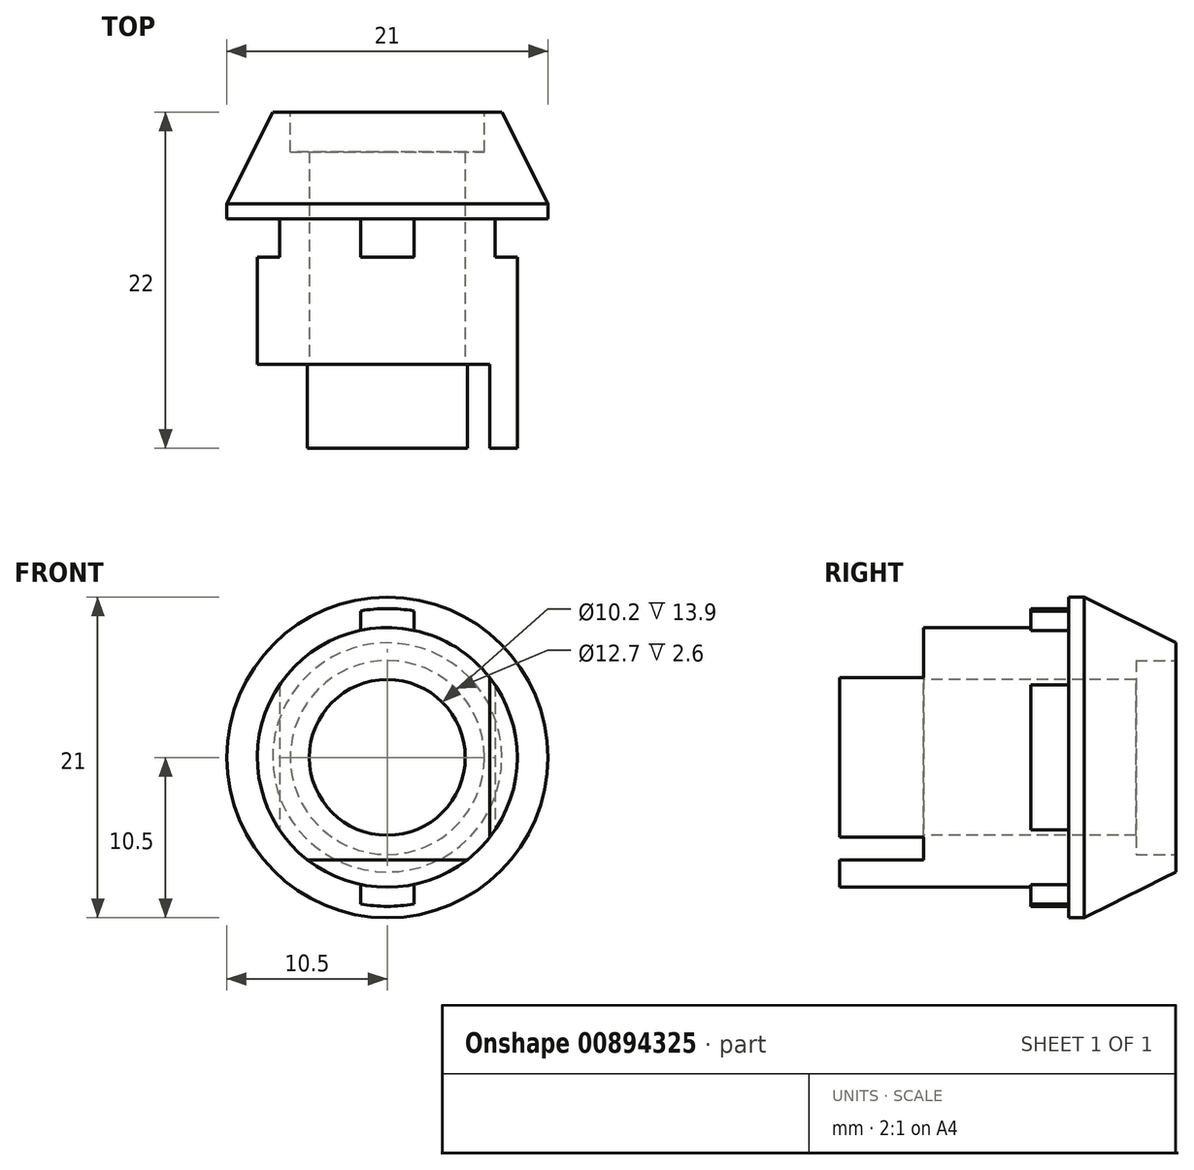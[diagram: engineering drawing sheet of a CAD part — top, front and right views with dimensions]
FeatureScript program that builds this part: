
annotation { "Feature Type Name" : "Feature", "Feature Type Description" : "" }
export const myFeature = defineFeature(function(context is Context, id is Id, definition is map)
    precondition{}
    {
        {
            var Q0;
            Q0=qCreatedBy(makeId("Front.planeOp"),FACE);
            var sketch = newSketch(context, id + "F0", { "sketchPlane" : qUnion([Q0])});
            skCircle(sketch, "E0", {"center": v(0, 0) * mm, "radius": 5.1 * mm});
            skCircle(sketch, "E1", {"center": v(0, 0) * mm, "radius": 10.5 * mm});
            skCircle(sketch, "E2", {"center": v(0, 0) * mm, "radius": 9.75 * mm});
            skCircle(sketch, "E3", {"center": v(0, 0) * mm, "radius": 8.5 * mm});
            skLineSegment(sketch, "E4", {"start": v(-1.75, 9.6) * mm, "end": v(-1.75, 8.32) * mm});
            skLineSegment(sketch, "E5.MirrorCS", {"start": v(1.75, 9.6) * mm, "end": v(1.75, 8.32) * mm});
            skLineSegment(sketch, "E6.MirrorCS", {"start": v(-1.75, -9.6) * mm, "end": v(-1.75, -8.32) * mm});
            skLineSegment(sketch, "E7.MirrorCS", {"start": v(1.75, -9.6) * mm, "end": v(1.75, -8.32) * mm});
            skLineSegment(sketch, "E8", {"start": v(7.05, 4.75) * mm, "end": v(7.05, -4.75) * mm});
            skLineSegment(sketch, "E9.MirrorCS", {"start": v(-7.05, 4.75) * mm, "end": v(-7.05, -4.75) * mm});
            skLineSegment(sketch, "E10", {"start": v(-5.23, -6.7) * mm, "end": v(5.23, -6.7) * mm});
            skLineSegment(sketch, "E11", {"start": v(6.7, -5.23) * mm, "end": v(6.7, 5.23) * mm});
            skSolve(sketch);
        }
        {
            var Q0;
            Q0=makeQuery(id+"F0.imprint","IMPRINT",FACE,{"disambiguationData":[TD([[makeQuery(id+"F0.imprint","IMPRINT",EDGE,{"derivedFrom":sQuery(id+"F0.wireOp",EDGE,"E1")}),1.0]])]});
            var Q1;
            {var subQ5=sQuery(id+"F0.wireOp",EDGE,"E4");Q1=makeQuery(id+"F0.imprint","IMPRINT",FACE,{"disambiguationData":[TD([[makeQuery(id+"F0.imprint","IMPRINT",EDGE,{"derivedFrom":subQ5}),-1.0]])]});}
            var Q2;
            {var subQ0=sQuery(id+"F0.wireOp",EDGE,"E4");Q2=makeQuery(id+"F0.imprint","IMPRINT",FACE,{"disambiguationData":[TD([[makeQuery(id+"F0.imprint","IMPRINT",EDGE,{"derivedFrom":subQ0}),1.0]])]});}
            var Q3;
            {var subQ3=sQuery(id+"F0.wireOp",EDGE,"E5.MirrorCS");Q3=makeQuery(id+"F0.imprint","IMPRINT",FACE,{"disambiguationData":[TD([[makeQuery(id+"F0.imprint","IMPRINT",EDGE,{"derivedFrom":subQ3}),1.0]])]});}
            var Q4;
            {var subQ0=sQuery(id+"F0.wireOp",EDGE,"E6.MirrorCS");Q4=makeQuery(id+"F0.imprint","IMPRINT",FACE,{"disambiguationData":[TD([[makeQuery(id+"F0.imprint","IMPRINT",EDGE,{"derivedFrom":subQ0}),-1.0]])]});}
            var Q5;
            {var subQ2=sQuery(id+"F0.wireOp",EDGE,"E10");Q5=makeQuery(id+"F0.imprint","IMPRINT",FACE,{"disambiguationData":[TD([[makeQuery(id+"F0.imprint","IMPRINT",EDGE,{"derivedFrom":subQ2}),-1.0]])]});}
            var Q6;
            {var subQ0=sQuery(id+"F0.wireOp",EDGE,"E9.MirrorCS");Q6=makeQuery(id+"F0.imprint","IMPRINT",FACE,{"disambiguationData":[TD([[makeQuery(id+"F0.imprint","IMPRINT",EDGE,{"derivedFrom":subQ0}),-1.0]])]});}
            var Q7;
            Q7=makeQuery(id+"F0.imprint","IMPRINT",FACE,{"disambiguationData":[TD([[makeQuery(id+"F0.imprint","IMPRINT",EDGE,{"derivedFrom":sQuery(id+"F0.wireOp",EDGE,"E0")}),-1.0]])]});
            var Q8;
            {var subQ0=sQuery(id+"F0.wireOp",EDGE,"E8");Q8=makeQuery(id+"F0.imprint","IMPRINT",FACE,{"disambiguationData":[TD([[makeQuery(id+"F0.imprint","IMPRINT",EDGE,{"derivedFrom":subQ0}),1.0]])]});}
            var Q9;
            {var subQ0=sQuery(id+"F0.wireOp",EDGE,"E8");Q9=makeQuery(id+"F0.imprint","IMPRINT",FACE,{"disambiguationData":[TD([[makeQuery(id+"F0.imprint","IMPRINT",EDGE,{"derivedFrom":subQ0}),-1.0]])]});}
            extrude(context, id + "F1", {"entities" : qUnion([Q0, Q1, Q2, Q3, Q4, Q5, Q6, Q7, Q8, Q9]), "depth" : -7 * mm, "offsetDistance" : 25 * mm});
        }
        {
            var Q0;
            {var subQ0=sQuery(id+"F0.wireOp",EDGE,"E4");Q0=makeQuery(id+"F0.imprint","IMPRINT",FACE,{"disambiguationData":[TD([[makeQuery(id+"F0.imprint","IMPRINT",EDGE,{"derivedFrom":subQ0}),1.0]])]});}
            var Q1;
            Q1=makeQuery(id+"F0.imprint","IMPRINT",FACE,{"disambiguationData":[TD([[makeQuery(id+"F0.imprint","IMPRINT",EDGE,{"derivedFrom":sQuery(id+"F0.wireOp",EDGE,"E0")}),-1.0]])]});
            var Q2;
            {var subQ0=sQuery(id+"F0.wireOp",EDGE,"E8");Q2=makeQuery(id+"F0.imprint","IMPRINT",FACE,{"disambiguationData":[TD([[makeQuery(id+"F0.imprint","IMPRINT",EDGE,{"derivedFrom":subQ0}),-1.0]])]});}
            var Q3;
            {var subQ0=sQuery(id+"F0.wireOp",EDGE,"E6.MirrorCS");Q3=makeQuery(id+"F0.imprint","IMPRINT",FACE,{"disambiguationData":[TD([[makeQuery(id+"F0.imprint","IMPRINT",EDGE,{"derivedFrom":subQ0}),-1.0]])]});}
            var Q4;
            {var subQ2=sQuery(id+"F0.wireOp",EDGE,"E10");Q4=makeQuery(id+"F0.imprint","IMPRINT",FACE,{"disambiguationData":[TD([[makeQuery(id+"F0.imprint","IMPRINT",EDGE,{"derivedFrom":subQ2}),-1.0]])]});}
            extrude(context, id + "F2", {"entities" : qUnion([Q0, Q1, Q2, Q3, Q4]), "operationType" : NewBodyOperationType.ADD, "depth" : 2.5 * mm, "offsetDistance" : 25 * mm});
        }
        {
            var Q0;
            {var subQ0=sQuery(id+"F0.wireOp",EDGE,"E9.MirrorCS");Q0=makeQuery(id+"F0.imprint","IMPRINT",FACE,{"disambiguationData":[TD([[makeQuery(id+"F0.imprint","IMPRINT",EDGE,{"derivedFrom":subQ0}),-1.0]])]});}
            var Q1;
            Q1=makeQuery(id+"F0.imprint","IMPRINT",FACE,{"disambiguationData":[TD([[makeQuery(id+"F0.imprint","IMPRINT",EDGE,{"derivedFrom":sQuery(id+"F0.wireOp",EDGE,"E0")}),-1.0]])]});
            var Q2;
            {var subQ0=sQuery(id+"F0.wireOp",EDGE,"E8");Q2=makeQuery(id+"F0.imprint","IMPRINT",FACE,{"disambiguationData":[TD([[makeQuery(id+"F0.imprint","IMPRINT",EDGE,{"derivedFrom":subQ0}),-1.0]])]});}
            var Q3;
            {var subQ0=sQuery(id+"F0.wireOp",EDGE,"E8");Q3=makeQuery(id+"F0.imprint","IMPRINT",FACE,{"disambiguationData":[TD([[makeQuery(id+"F0.imprint","IMPRINT",EDGE,{"derivedFrom":subQ0}),1.0]])]});}
            var Q4;
            {var subQ2=sQuery(id+"F0.wireOp",EDGE,"E10");Q4=makeQuery(id+"F0.imprint","IMPRINT",FACE,{"disambiguationData":[TD([[makeQuery(id+"F0.imprint","IMPRINT",EDGE,{"derivedFrom":subQ2}),-1.0]])]});}
            extrude(context, id + "F3", {"entities" : qUnion([Q0, Q1, Q2, Q3, Q4]), "operationType" : NewBodyOperationType.ADD, "depth" : 9.5 * mm, "offsetDistance" : 25 * mm, "hasSecondDirection" : true, "secondDirectionOppositeDirection" : false, "secondDirectionDepth" : 2.5 * mm});
        }
        {
            var Q0;
            {var subQ2=sQuery(id+"F0.wireOp",EDGE,"E10");Q0=makeQuery(id+"F0.imprint","IMPRINT",FACE,{"disambiguationData":[TD([[makeQuery(id+"F0.imprint","IMPRINT",EDGE,{"derivedFrom":subQ2}),-1.0]])]});}
            var Q1;
            {var subQ0=sQuery(id+"F0.wireOp",EDGE,"E8");Q1=makeQuery(id+"F0.imprint","IMPRINT",FACE,{"disambiguationData":[TD([[makeQuery(id+"F0.imprint","IMPRINT",EDGE,{"derivedFrom":subQ0}),-1.0]])]});}
            var Q2;
            {var subQ0=sQuery(id+"F0.wireOp",EDGE,"E8");Q2=makeQuery(id+"F0.imprint","IMPRINT",FACE,{"disambiguationData":[TD([[makeQuery(id+"F0.imprint","IMPRINT",EDGE,{"derivedFrom":subQ0}),1.0]])]});}
            extrude(context, id + "F4", {"entities" : qUnion([Q0, Q1, Q2]), "operationType" : NewBodyOperationType.ADD, "depth" : 15 * mm, "offsetDistance" : 25 * mm, "hasSecondDirection" : true, "secondDirectionOppositeDirection" : false, "secondDirectionDepth" : 7 * mm});
        }
        {
            var Q0;
            Q0=makeQuery(id+"F1.opExtrude","CAP_FACE",FACE,{"disambiguationData":[OSD([sQuery(id+"F0.wireOp",EDGE,"E0"),sQuery(id+"F0.wireOp",EDGE,"E1")])],"isStart":false});
            var sketch = newSketch(context, id + "F5", { "sketchPlane" : qUnion([Q0])});
            skCircle(sketch, "E12", {"center": v(0, 0) * mm, "radius": 6.35 * mm});
            skSolve(sketch);
        }
        {
            var Q0;
            Q0=makeQuery(id+"F5.imprint","IMPRINT",FACE,{"disambiguationData":[TD([[makeQuery(id+"F5.imprint","IMPRINT",EDGE,{"derivedFrom":sQuery(id+"F5.wireOp",EDGE,"E12")}),1.0]])]});
            extrude(context, id + "F6", {"entities" : qUnion([Q0]), "operationType" : NewBodyOperationType.REMOVE, "oppositeDirection" : true, "depth" : 2.6 * mm, "offsetDistance" : 25 * mm});
        }
        {
            var Q0;
            Q0=makeQuery(id+"F1.opExtrude","CAP_EDGE",EDGE,{"disambiguationData":[OSD([sQuery(id+"F0.wireOp",EDGE,"E1")])],"isStart":false});
            chamfer(context, id + "F7", {"entities" : qUnion([Q0]), "chamferType" : ChamferType.TWO_OFFSETS, "width1" : 3 * mm, "oppositeDirection" : true, "width2" : 6 * mm, "tangentPropagation" : true});
        }
    });
